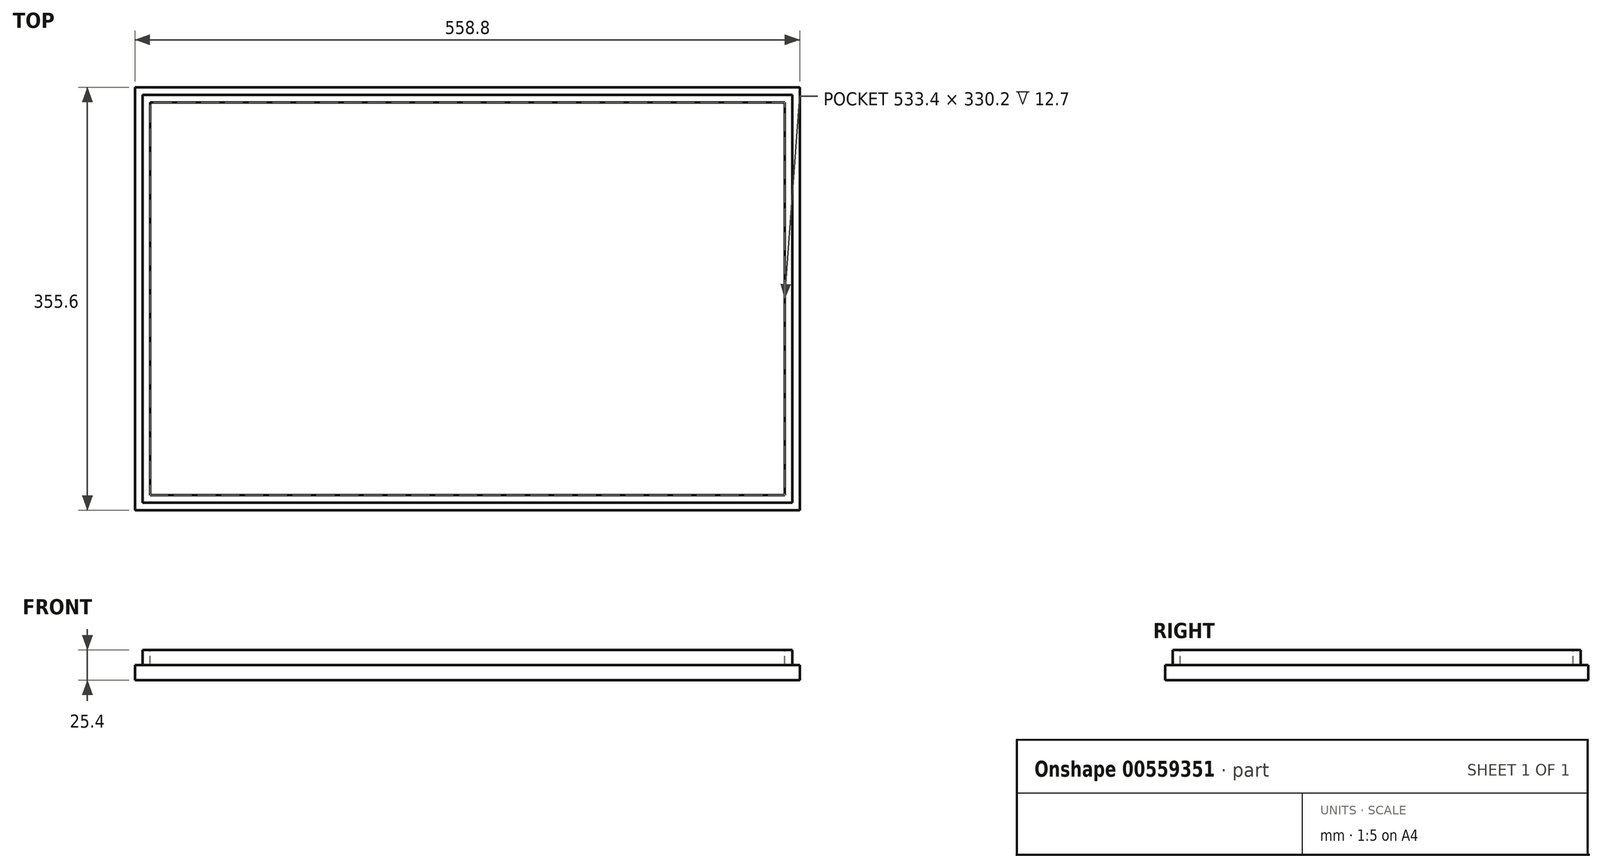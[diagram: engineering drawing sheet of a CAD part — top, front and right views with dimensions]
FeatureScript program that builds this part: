
annotation { "Feature Type Name" : "Feature", "Feature Type Description" : "" }
export const myFeature = defineFeature(function(context is Context, id is Id, definition is map)
    precondition{}
    {
        {
            var Q0;
            Q0=qCreatedBy(makeId("Top.planeOp"),FACE);
            var sketch = newSketch(context, id + "F0", { "sketchPlane" : qUnion([Q0])});
            skLineSegment(sketch, "E0.bottom", {"start": v(-266.92, 178.67) * mm, "end": v(291.88, 178.67) * mm});
            skLineSegment(sketch, "E0.top", {"start": v(-266.92, -176.93) * mm, "end": v(291.88, -176.93) * mm});
            skLineSegment(sketch, "E0.left", {"start": v(-266.92, 178.67) * mm, "end": v(-266.92, -176.93) * mm});
            skLineSegment(sketch, "E0.right", {"start": v(291.88, 178.67) * mm, "end": v(291.88, -176.93) * mm});
            skSolve(sketch);
        }
        {
            var Q0;
            Q0=makeQuery(id+"F0.imprint","IMPRINT",FACE,{"disambiguationData":[TD([[makeQuery(id+"F0.imprint","IMPRINT",EDGE,{"derivedFrom":sQuery(id+"F0.wireOp",EDGE,"E0.bottom")}),-1.0]])]});
            extrude(context, id + "F1", {"entities" : qUnion([Q0]), "depth" : 25.4 * mm, "offsetDistance" : 25.4 * mm});
        }
        {
            var Q0;
            Q0=makeQuery(id+"F1.opExtrude","CAP_FACE",FACE,{"disambiguationData":[OSD([sQuery(id+"F0.wireOp",EDGE,"E0.bottom"),sQuery(id+"F0.wireOp",EDGE,"E0.top"),sQuery(id+"F0.wireOp",EDGE,"E0.left"),sQuery(id+"F0.wireOp",EDGE,"E0.right")])],"isStart":false});
            var sketch = newSketch(context, id + "F2", { "sketchPlane" : qUnion([Q0])});
            skLineSegment(sketch, "E1.bottom", {"start": v(-254.22, 165.97) * mm, "end": v(279.18, 165.97) * mm});
            skLineSegment(sketch, "E1.top", {"start": v(-254.22, -164.23) * mm, "end": v(279.18, -164.23) * mm});
            skLineSegment(sketch, "E1.left", {"start": v(-254.22, 165.97) * mm, "end": v(-254.22, -164.23) * mm});
            skLineSegment(sketch, "E1.right", {"start": v(279.18, 165.97) * mm, "end": v(279.18, -164.23) * mm});
            skSolve(sketch);
        }
        {
            var Q0;
            Q0=makeQuery(id+"F2.imprint","IMPRINT",FACE,{"disambiguationData":[TD([[makeQuery(id+"F2.imprint","IMPRINT",EDGE,{"derivedFrom":sQuery(id+"F2.wireOp",EDGE,"E1.bottom")}),-1.0]])]});
            extrude(context, id + "F3", {"entities" : qUnion([Q0]), "operationType" : NewBodyOperationType.REMOVE, "oppositeDirection" : true, "depth" : 12.7 * mm, "offsetDistance" : 25.4 * mm});
        }
        {
            var Q0;
            Q0=makeQuery(id+"F1.opExtrude","CAP_FACE",FACE,{"disambiguationData":[OSD([sQuery(id+"F0.wireOp",EDGE,"E0.bottom"),sQuery(id+"F0.wireOp",EDGE,"E0.top"),sQuery(id+"F0.wireOp",EDGE,"E0.left"),sQuery(id+"F0.wireOp",EDGE,"E0.right")])],"isStart":false});
            var sketch = newSketch(context, id + "F4", { "sketchPlane" : qUnion([Q0])});
            skLineSegment(sketch, "E2.0.0", {"start": v(-254.22, 165.97) * mm, "end": v(-254.22, -164.23) * mm});
            skLineSegment(sketch, "E2.0.1", {"start": v(-254.22, -164.23) * mm, "end": v(279.18, -164.23) * mm});
            skLineSegment(sketch, "E2.0.2", {"start": v(279.18, -164.23) * mm, "end": v(279.18, 165.97) * mm});
            skLineSegment(sketch, "E2.0.3", {"start": v(279.18, 165.97) * mm, "end": v(-254.22, 165.97) * mm});
            skLineSegment(sketch, "E3.0", {"start": v(-266.92, 178.67) * mm, "end": v(291.88, 178.67) * mm});
            skLineSegment(sketch, "E4.0", {"start": v(-266.92, 178.67) * mm, "end": v(-266.92, -176.93) * mm});
            skLineSegment(sketch, "E5.0", {"start": v(-266.92, -176.93) * mm, "end": v(291.88, -176.93) * mm});
            skLineSegment(sketch, "E6.0", {"start": v(291.88, 178.67) * mm, "end": v(291.88, -176.93) * mm});
            skLineSegment(sketch, "E7.bottom", {"start": v(-260.57, 172.32) * mm, "end": v(285.53, 172.32) * mm});
            skLineSegment(sketch, "E7.top", {"start": v(-260.57, -170.58) * mm, "end": v(285.53, -170.58) * mm});
            skLineSegment(sketch, "E7.left", {"start": v(-260.57, 172.32) * mm, "end": v(-260.57, -170.58) * mm});
            skLineSegment(sketch, "E7.right", {"start": v(285.53, 172.32) * mm, "end": v(285.53, -170.58) * mm});
            skSolve(sketch);
        }
        {
            var Q0;
            Q0=makeQuery(id+"F4.imprint","IMPRINT",FACE,{"disambiguationData":[TD([[makeQuery(id+"F4.imprint","IMPRINT",EDGE,{"derivedFrom":sQuery(id+"F4.wireOp",EDGE,"E3.0")}),-1.0]])]});
            extrude(context, id + "F5", {"entities" : qUnion([Q0]), "operationType" : NewBodyOperationType.REMOVE, "oppositeDirection" : true, "depth" : 12.7 * mm, "offsetDistance" : 25.4 * mm});
        }
    });
